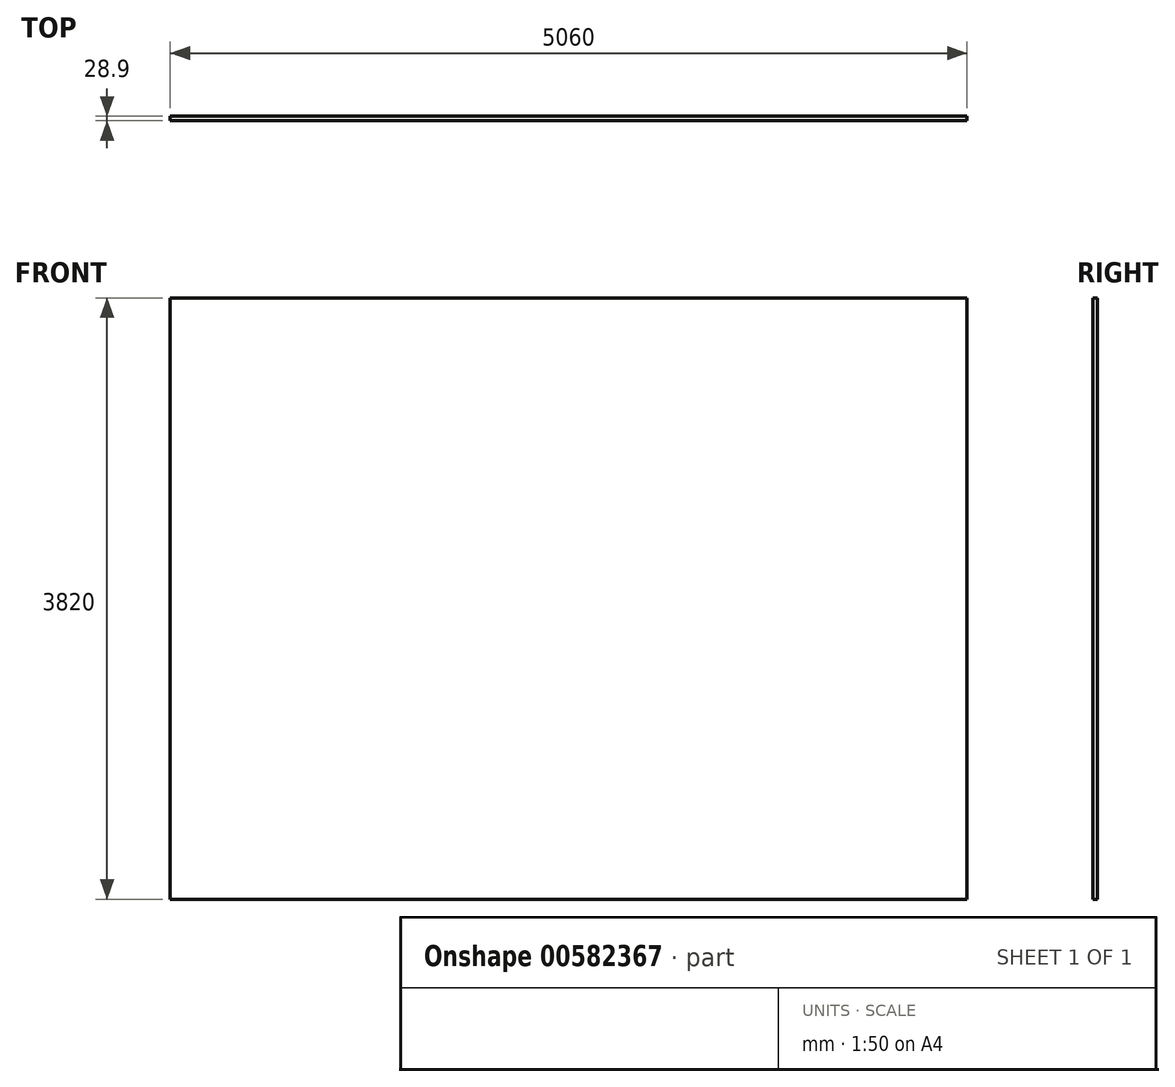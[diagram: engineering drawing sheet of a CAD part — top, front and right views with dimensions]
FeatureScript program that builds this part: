
annotation { "Feature Type Name" : "Feature", "Feature Type Description" : "" }
export const myFeature = defineFeature(function(context is Context, id is Id, definition is map)
    precondition{}
    {
        {
            var Q0;
            Q0=qCreatedBy(makeId("Front.planeOp"),FACE);
            var sketch = newSketch(context, id + "F0", { "sketchPlane" : qUnion([Q0])});
            skLineSegment(sketch, "E0.bottom", {"start": v(0, 0) * mm, "end": v(5060, 0) * mm});
            skLineSegment(sketch, "E0.top", {"start": v(0, 3820) * mm, "end": v(5060, 3820) * mm});
            skLineSegment(sketch, "E0.left", {"start": v(0, 0) * mm, "end": v(0, 3820) * mm});
            skLineSegment(sketch, "E0.right", {"start": v(5060, 0) * mm, "end": v(5060, 3820) * mm});
            skSolve(sketch);
        }
        {
            var Q0;
            Q0=makeQuery(id+"F0.imprint","IMPRINT",FACE,{"disambiguationData":[TD([[makeQuery(id+"F0.imprint","IMPRINT",EDGE,{"derivedFrom":sQuery(id+"F0.wireOp",EDGE,"E0.bottom")}),1.0]])]});
            extrude(context, id + "F1", {"entities" : qUnion([Q0]), "depth" : 28.9 * mm, "offsetDistance" : 25 * mm});
        }
    });
